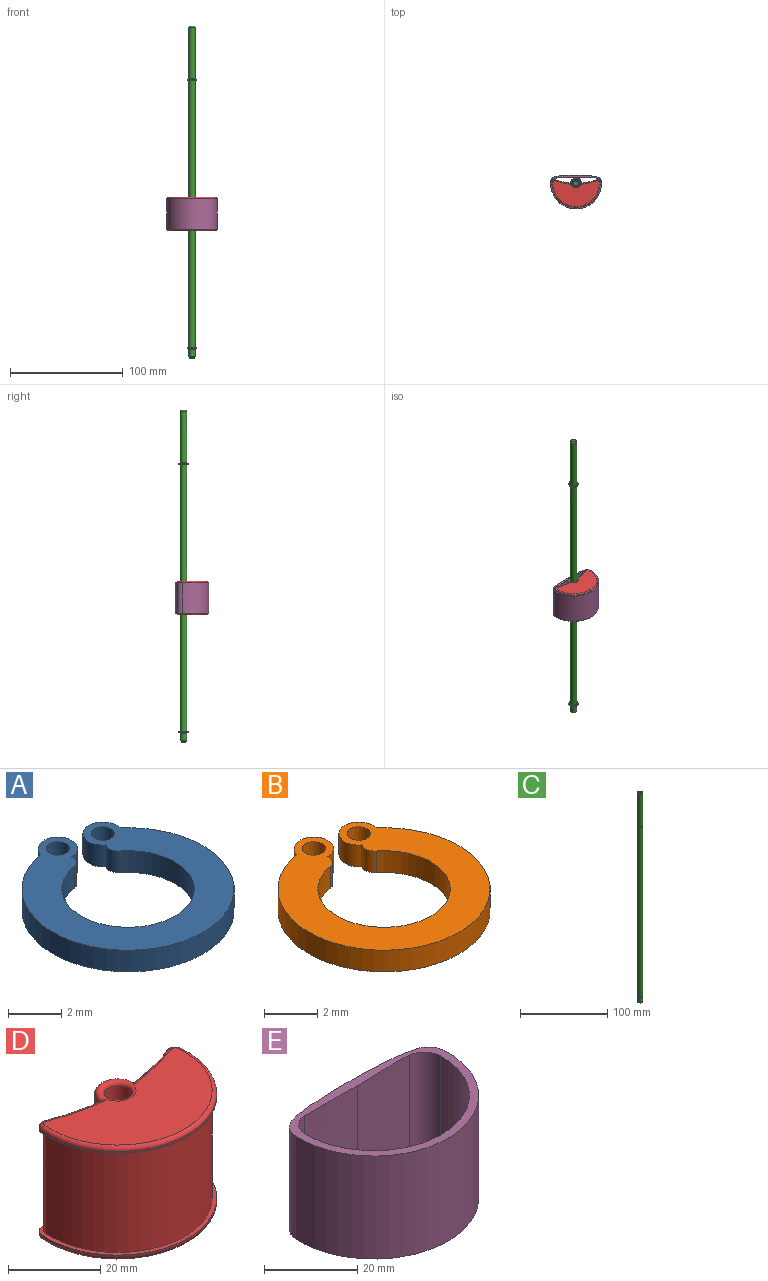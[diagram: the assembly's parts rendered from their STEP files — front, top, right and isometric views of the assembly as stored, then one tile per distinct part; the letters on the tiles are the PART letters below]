
ASSEMBLY  parts=5 mates=4
PART A: 12 faces, bbox 8x8.5x1 mm
  f0: plane 1x0.04mm, normal (1,0,0), area 0mm2, adj f1,f8,f10,f11
  f1: cylinder r=0.75mm len=1.5mm, axis (0,0,-1), area 3.3mm2, adj f0,f2,f10,f11
  f2: cylinder r=4mm len=8mm, axis (0,0,-1), area 21.6mm2, adj f1,f3,f10,f11
  f3: cylinder r=0.75mm len=1.5mm, axis (0,0,-1), area 3.3mm2, adj f2,f4,f10,f11
  f4: plane 1x0.01mm, normal (-0.84,0.54,0), area 0mm2, adj f3,f5,f10,f11
  f5: cylinder r=0.5mm len=1mm, axis (0,0,-1), area 0.7mm2, adj f4,f6,f10,f11
  f6: cylinder r=2.5mm len=5mm, axis (0,0,-1), area 13.6mm2, adj f5,f8,f10,f11
  f7: cylinder r=0.44mm len=1mm, axis (0,0,-1), area 2.8mm2, adj f10,f11
  f8: cylinder r=0.5mm len=1mm, axis (0,0,-1), area 0.7mm2, adj f0,f6,f10,f11
  f9: cylinder r=0.44mm len=1mm, axis (0,0,-1), area 2.8mm2, adj f10,f11
  f10: plane 8.49x8mm, normal (0,0,1), area 29.1mm2, adj f0,f1,f2,f3,f4,f5,f6,f7
  f11: plane 8.49x8mm, normal (0,0,-1), area 29.1mm2, adj f0,f1,f2,f3,f4,f5,f6,f7
PART B: 12 faces, bbox 8x8.5x1 mm
  f0: plane 1x0.04mm, normal (1,0,0), area 0mm2, adj f1,f8,f10,f11
  f1: cylinder r=0.75mm len=1.5mm, axis (0,0,-1), area 3.3mm2, adj f0,f2,f10,f11
  f2: cylinder r=4mm len=8mm, axis (0,0,-1), area 21.6mm2, adj f1,f3,f10,f11
  f3: cylinder r=0.75mm len=1.5mm, axis (0,0,-1), area 3.3mm2, adj f2,f4,f10,f11
  f4: plane 1x0.01mm, normal (-0.84,0.54,0), area 0mm2, adj f3,f5,f10,f11
  f5: cylinder r=0.5mm len=1mm, axis (0,0,-1), area 0.7mm2, adj f4,f6,f10,f11
  f6: cylinder r=2.5mm len=5mm, axis (0,0,-1), area 13.6mm2, adj f5,f8,f10,f11
  f7: cylinder r=0.44mm len=1mm, axis (0,0,-1), area 2.8mm2, adj f10,f11
  f8: cylinder r=0.5mm len=1mm, axis (0,0,-1), area 0.7mm2, adj f0,f6,f10,f11
  f9: cylinder r=0.44mm len=1mm, axis (0,0,-1), area 2.8mm2, adj f10,f11
  f10: plane 8.49x8mm, normal (0,0,1), area 29.1mm2, adj f0,f1,f2,f3,f4,f5,f6,f7
  f11: plane 8.49x8mm, normal (0,0,-1), area 29.1mm2, adj f0,f1,f2,f3,f4,f5,f6,f7
PART C: 9 faces, bbox 7.6x7.6x294 mm
  f0: cylinder r=3mm len=6.75mm, axis (0,0,-1), area 127.2mm2, adj f2,f3
  f1: plane 4x4mm, normal (0,0,-1), area 12.6mm2, adj f2
  f2: cone r=3mm half-angle=45deg, axis (0,0,1), area 22.2mm2, adj f0,f1
  f3: torus R=3mm, axis (0,0,-1), area 37.3mm2, adj f0,f4
  f4: cylinder r=3mm len=236.5mm, axis (0,0,-1), area 4457.9mm2, adj f3,f5
  f5: torus R=3mm, axis (0,0,-1), area 37.3mm2, adj f4,f8
  f6: plane 4x4mm, normal (0,0,1), area 12.6mm2, adj f7
  f7: cone r=2mm half-angle=45deg, axis (0,0,-1), area 22.2mm2, adj f6,f8
  f8: cylinder r=3mm len=45.75mm, axis (0,0,-1), area 862.4mm2, adj f5,f7
PART D: 29 faces, bbox 46.5x28.7x30 mm
  f0: cylinder r=50mm len=28mm, axis (0,0,-1), area 368.7mm2, adj f3,f9,f10,f11,f14,f16,f18,f24
  f1: cylinder r=50mm len=28mm, axis (0,0,-1), area 368.7mm2, adj f3,f9,f10,f12,f13,f15,f20,f27
  f2: cylinder r=21.5mm len=43mm, axis (0,0,-1), area 35.7mm2, adj f9,f13,f14,f26
  f3: cylinder r=5mm len=28mm, axis (0,0,-1), area 425.8mm2, adj f0,f1,f17,f23
  f4: cylinder r=21.5mm len=43mm, axis (0,0,-1), area 35.7mm2, adj f10,f15,f16,f21
  f5: cylinder r=3mm len=28mm, axis (0,0,-1), area 527.8mm2, adj f17,f23
  f6: plane 41x23.26mm, normal (0,0,1), area 657.9mm2, adj f17,f18,f19,f20,f21,f22
  f7: plane 41x23.26mm, normal (0,0,-1), area 657.9mm2, adj f23,f24,f25,f26,f27,f28
  f8: cylinder r=20.5mm len=41mm, axis (0,0,1), area 1821.7mm2, adj f9,f10,f11,f12
  f9: plane 43x25.26mm, normal (0,0,1), area 74.8mm2, adj f0,f1,f2,f8,f11,f12,f13,f14
  f10: plane 43x25.26mm, normal (0,0,-1), area 74.8mm2, adj f0,f1,f4,f8,f11,f12,f15,f16
  f11: cylinder r=2mm len=27mm, axis (0,0,-1), area 100.4mm2, adj f0,f8,f9,f10
  f12: cylinder r=2mm len=27mm, axis (0,0,-1), area 100.4mm2, adj f1,f8,f9,f10
  f13: cylinder r=2mm len=2.74mm, axis (0,0,1), area 1.9mm2, adj f1,f2,f9,f28
  f14: cylinder r=2mm len=2.74mm, axis (0,0,1), area 1.9mm2, adj f0,f2,f9,f25
  f15: cylinder r=2mm len=2.74mm, axis (0,0,1), area 1.9mm2, adj f1,f4,f10,f22
  f16: cylinder r=2mm len=2.74mm, axis (0,0,1), area 1.9mm2, adj f0,f4,f10,f19
  f17: torus R=4mm, axis (0,0,1), area 56.5mm2, adj f3,f5,f6,f18,f20
  f18: torus R=51mm, axis (0,0,1), area 23mm2, adj f0,f6,f17,f19
  f19: torus R=1mm, axis (0,0,1), area 4.8mm2, adj f6,f16,f18,f21
  f20: torus R=51mm, axis (0,0,1), area 23mm2, adj f1,f6,f17,f22
  f21: torus R=20.5mm, axis (0,0,1), area 110.3mm2, adj f4,f6,f19,f22
  f22: torus R=1mm, axis (0,0,1), area 4.8mm2, adj f6,f15,f20,f21
  f23: torus R=4mm, axis (0,0,1), area 56.5mm2, adj f3,f5,f7,f24,f27
  f24: torus R=51mm, axis (0,0,1), area 23mm2, adj f0,f7,f23,f25
  f25: torus R=1mm, axis (0,0,1), area 4.8mm2, adj f7,f14,f24,f26
  f26: torus R=20.5mm, axis (0,0,1), area 110.3mm2, adj f2,f7,f25,f28
  f27: torus R=51mm, axis (0,0,1), area 23mm2, adj f1,f7,f23,f28
  f28: torus R=1mm, axis (0,0,1), area 4.8mm2, adj f7,f13,f26,f27
PART E: 11 faces, bbox 45x30.2x27 mm
  f0: extruded ~37.9x27mm, area 1030.6mm2, adj f5,f6,f9,f10
  f1: extruded ~27x15.98mm, area 431.8mm2, adj f3,f5,f6,f7
  f2: cylinder r=20.5mm len=41mm, axis (0,0,-1), area 1754.2mm2, adj f5,f6,f7,f8
  f3: extruded ~27x15.9mm, area 429.5mm2, adj f1,f5,f6,f8
  f4: cylinder r=22.5mm len=45mm, axis (0,0,-1), area 1974.2mm2, adj f5,f6,f9,f10
  f5: plane 45x30.24mm, normal (0,0,1), area 229.1mm2, adj f0,f1,f2,f3,f4,f7,f8,f9
  f6: plane 45x30.24mm, normal (0,0,-1), area 229.1mm2, adj f0,f1,f2,f3,f4,f7,f8,f9
  f7: cylinder r=5mm len=27mm, axis (0,0,-1), area 197.3mm2, adj f1,f2,f5,f6
  f8: cylinder r=5mm len=27mm, axis (0,0,-1), area 199.1mm2, adj f2,f3,f5,f6
  f9: cylinder r=5mm len=27mm, axis (0,0,-1), area 162.7mm2, adj f0,f4,f5,f6
  f10: cylinder r=5mm len=27mm, axis (0,0,-1), area 165.9mm2, adj f0,f4,f5,f6
PLACE A t=(-55.87,8.06,-2.81)mm
PLACE B t=(-55.87,8.06,-2.81)mm
PLACE C t=(-55.87,8.06,-2.81)mm
PLACE D t=(-55.87,8.06,-22.31)mm
PLACE E t=(-55.87,8.06,-22.31)mm
MATE fastened C.f3 <-> A.f6  axis (0,0,-1) through (-55.87,8.06,-141.31)mm
MATE fastened E.f2 <-> D.f8  axis (0,0,1) through (-55.87,8.06,-8.81)mm
MATE fastened C.f0 <-> D.f3  axis (0,0,-1) through (-55.87,8.06,-22.31)mm
MATE fastened C.f3 <-> B.f6  axis (0,0,-1) through (-55.87,8.06,96.69)mm
